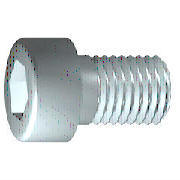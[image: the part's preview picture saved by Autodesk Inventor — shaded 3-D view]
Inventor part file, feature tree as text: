
AUTODESK INVENTOR PART (.ipt)
format: ipt  version: 2024 (Build 280153000, 153)  size: 185,344 bytes
history: native  units: mm (DEFAULTED — no unit token found)
features: fillet x2, sketch x2, extrude x1, thread x1, chamfer x1, plane x1
ambient origin geometry x7: Origin, YZ Plane, XY Plane, X Axis, Y Axis, Z Axis, Center Point
bodies: Solid1 (feature_tree), Body (feature_tree)
feature tree (8):
  extrude  "Slot"  Depth=2.0mm
  fillet  "Fillet1"  Radius=4.0mm
  thread  "Thread"  [1 undecoded]
  chamfer  "Chamfer1"  Distance=4.0mm
  plane  "Work Plane1"
  fillet  "Fillet2"  Radius=4.0mm
  sketch  "Sketch1"  dims[d1=20.0mm d2=0.429515mm d3=4.0mm d4=2.0mm]
  sketch  "Sketch2"  dims[d5=60.0deg d6=4.0mm d7=4.0mm d8=3.464102mm d9=7.0mm d10=90.0deg d11=10.0mm d12=0.0mm d13=20.0mm d14=0.0mm d15=0.429415mm d16=0.429415mm d17=0.4mm d19=0.0mm d26=35.0mm d27=45.0deg d28=0.0mm d29=0.0mm d30=0.1mm]
note: 1 required parameter value undecoded (feature->parameter linkage not recoverable at this tier; creation-order binding heuristic only, values carry confidence <= 0.55)
